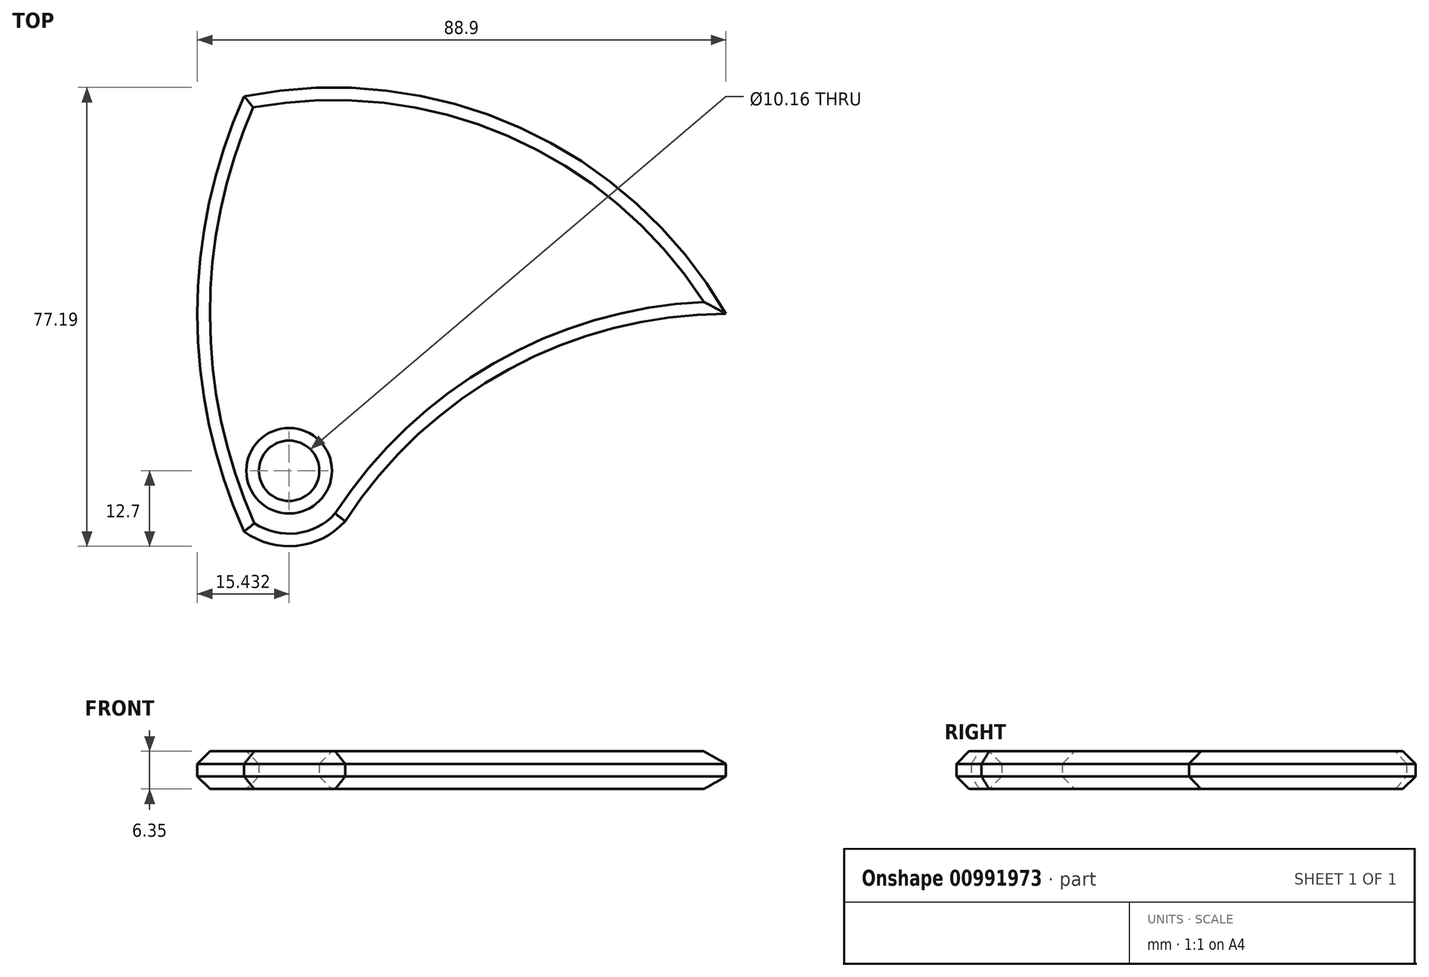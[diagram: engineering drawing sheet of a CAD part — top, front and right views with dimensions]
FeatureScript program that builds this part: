
annotation { "Feature Type Name" : "Feature", "Feature Type Description" : "" }
export const myFeature = defineFeature(function(context is Context, id is Id, definition is map)
    precondition{}
    {
        {
            var Q0;
            Q0=qCreatedBy(makeId("Top.planeOp"),FACE);
            var sketch = newSketch(context, id + "F0", { "sketchPlane" : qUnion([Q0])});
            skCircle(sketch, "E0", {"center": v(0, 0) * mm, "radius": 76.2 * mm});
            skArc(sketch, "E1", {"start": v(0, 0) * mm, "mid": v(10.2, 38.1) * mm, "end": v(0, 76.2) * mm});
            skLineSegment(sketch, "E2", {"start": v(0, 76.2) * mm, "end": v(0, 0) * mm, "construction": true});
            skLineSegment(sketch, "E3", {"start": v(0, 0) * mm, "end": v(66, 38.1) * mm, "construction": true});
            skLineSegment(sketch, "E4", {"start": v(0, 0) * mm, "end": v(66, -38.1) * mm, "construction": true});
            skLineSegment(sketch, "E5", {"start": v(0, 0) * mm, "end": v(0, -76.2) * mm, "construction": true});
            skLineSegment(sketch, "E6", {"start": v(0, 0) * mm, "end": v(-66, -38.1) * mm, "construction": true});
            skLineSegment(sketch, "E7", {"start": v(0, 0) * mm, "end": v(-66, 38.1) * mm, "construction": true});
            skArc(sketch, "E8", {"start": v(0, 0) * mm, "mid": v(38.1, 10.2) * mm, "end": v(66, 38.1) * mm});
            skArc(sketch, "E9", {"start": v(0, 0) * mm, "mid": v(27.9, -27.9) * mm, "end": v(66, -38.1) * mm});
            skArc(sketch, "E10", {"start": v(0, 0) * mm, "mid": v(-10.2, -38.1) * mm, "end": v(0, -76.2) * mm});
            skArc(sketch, "E11", {"start": v(0, 0) * mm, "mid": v(-38.1, -10.2) * mm, "end": v(-66, -38.1) * mm});
            skArc(sketch, "E12", {"start": v(0, 0) * mm, "mid": v(-27.9, 27.9) * mm, "end": v(-66, 38.1) * mm});
            skSolve(sketch);
        }
        {
            var Q0;
            Q0=qCreatedBy(makeId("Top.planeOp"),FACE);
            var sketch = newSketch(context, id + "F1", { "sketchPlane" : qUnion([Q0])});
            skCircle(sketch, "E13", {"center": v(0, 0) * mm, "radius": 76.2 * mm});
            skArc(sketch, "E14", {"start": v(-72.2, 51.86) * mm, "mid": v(-69.44, 44.82) * mm, "end": v(-66, 38.1) * mm, "construction": true});
            skArc(sketch, "E15", {"start": v(8.8, 88.46) * mm, "mid": v(4.1, 82.55) * mm, "end": v(0, 76.2) * mm, "construction": true});
            skArc(sketch, "E16", {"start": v(81.01, 36.6) * mm, "mid": v(73.54, 37.73) * mm, "end": v(66, 38.1) * mm, "construction": true});
            skArc(sketch, "E17", {"start": v(72.2, -51.86) * mm, "mid": v(69.44, -44.82) * mm, "end": v(66, -38.1) * mm, "construction": true});
            skArc(sketch, "E18", {"start": v(-8.8, -88.46) * mm, "mid": v(-4.1, -82.55) * mm, "end": v(0, -76.2) * mm, "construction": true});
            skArc(sketch, "E19", {"start": v(-81.01, -36.6) * mm, "mid": v(-73.54, -37.73) * mm, "end": v(-66, -38.1) * mm, "construction": true});
            skCircle(sketch, "E20", {"center": v(0, 0) * mm, "radius": 88.9 * mm, "construction": true});
            skArc(sketch, "E21.trimOffspring", {"start": v(0, 0) * mm, "mid": v(34.62, -31.34) * mm, "end": v(81.01, -36.6) * mm, "construction": true});
            skArc(sketch, "E22.trimOffspring", {"start": v(0, 0) * mm, "mid": v(-9.83, -45.65) * mm, "end": v(8.8, -88.46) * mm, "construction": true});
            skArc(sketch, "E23.trimOffspring", {"start": v(0, 0) * mm, "mid": v(-44.45, -14.3) * mm, "end": v(-72.2, -51.86) * mm, "construction": true});
            skArc(sketch, "E24.trimOffspring", {"start": v(0, 0) * mm, "mid": v(-34.62, 31.34) * mm, "end": v(-81.01, 36.6) * mm, "construction": true});
            skArc(sketch, "E25.trimOffspring", {"start": v(0, 0) * mm, "mid": v(9.83, 45.65) * mm, "end": v(-8.8, 88.46) * mm, "construction": true});
            skArc(sketch, "E26.trimOffspring", {"start": v(0, 0) * mm, "mid": v(44.45, 14.3) * mm, "end": v(72.2, 51.86) * mm, "construction": true});
            skLineSegment(sketch, "E27", {"start": v(0, 88.9) * mm, "end": v(0, 0) * mm, "construction": true});
            skLineSegment(sketch, "E28", {"start": v(-15.44, 87.55) * mm, "end": v(0, 0) * mm, "construction": true});
            skLineSegment(sketch, "E29", {"start": v(0, 0) * mm, "end": v(-83.54, 30.4) * mm, "construction": true});
            skLineSegment(sketch, "E30", {"start": v(0, 0) * mm, "end": v(-68.1, -57.14) * mm, "construction": true});
            skLineSegment(sketch, "E31", {"start": v(0, 0) * mm, "end": v(15.44, -87.55) * mm, "construction": true});
            skLineSegment(sketch, "E32", {"start": v(0, 0) * mm, "end": v(83.54, -30.4) * mm, "construction": true});
            skLineSegment(sketch, "E33", {"start": v(0, 0) * mm, "end": v(68.1, 57.14) * mm, "construction": true});
            skCircle(sketch, "E34", {"center": v(0, 0) * mm, "radius": 82.55 * mm, "construction": true});
            skArc(sketch, "E35", {"start": v(-60.5, -34.92) * mm, "mid": v(61.3, 33.48) * mm, "end": v(-62.08, -32.01) * mm, "construction": true});
            skLineSegment(sketch, "E36.0", {"start": v(0, 0) * mm, "end": v(-66, 38.1) * mm, "construction": true});
            skPoint(sketch, "E37.0", {"position": v(33, 19.05) * mm});
            skLineSegment(sketch, "E38.0", {"start": v(0, 0) * mm, "end": v(66, 38.1) * mm, "construction": true});
            skLineSegment(sketch, "E39.0", {"start": v(0, 0) * mm, "end": v(66, -38.1) * mm, "construction": true});
            skLineSegment(sketch, "E40.0", {"start": v(0, 0) * mm, "end": v(0, -76.2) * mm, "construction": true});
            skLineSegment(sketch, "E41.0", {"start": v(0, 0) * mm, "end": v(-66, -38.1) * mm, "construction": true});
            skLineSegment(sketch, "E42", {"start": v(-66, 38.1) * mm, "end": v(-76.99, 44.45) * mm, "construction": true});
            skArc(sketch, "E43", {"start": v(-72.2, 51.86) * mm, "mid": v(-68.78, 41.67) * mm, "end": v(-58.77, 37.76) * mm, "construction": true});
            skArc(sketch, "E44", {"start": v(8.8, 88.46) * mm, "mid": v(1.7, 80.4) * mm, "end": v(3.32, 69.77) * mm, "construction": true});
            skArc(sketch, "E45", {"start": v(81.01, 36.6) * mm, "mid": v(70.48, 38.73) * mm, "end": v(62.08, 32.01) * mm, "construction": true});
            skArc(sketch, "E46", {"start": v(72.2, -51.86) * mm, "mid": v(68.78, -41.67) * mm, "end": v(58.77, -37.76) * mm, "construction": true});
            skArc(sketch, "E47", {"start": v(-8.8, -88.46) * mm, "mid": v(-1.7, -80.4) * mm, "end": v(-3.32, -69.77) * mm, "construction": true});
            skArc(sketch, "E48", {"start": v(-81.01, -36.6) * mm, "mid": v(-70.48, -38.73) * mm, "end": v(-62.08, -32.01) * mm, "construction": true});
            skArc(sketch, "E49", {"start": v(0, 0) * mm, "mid": v(-44.45, -14.3) * mm, "end": v(-72.2, -51.86) * mm});
            skArc(sketch, "E50", {"start": v(-81.01, -36.6) * mm, "mid": v(-70.48, -38.73) * mm, "end": v(-62.08, -32.01) * mm});
            skArc(sketch, "E51", {"start": v(0, 0) * mm, "mid": v(-34.62, 31.34) * mm, "end": v(-81.01, 36.6) * mm});
            skArc(sketch, "E52", {"start": v(-81.01, 36.6) * mm, "mid": v(-88.46, -8.8) * mm, "end": v(-72.2, -51.86) * mm});
            skCircle(sketch, "E53", {"center": v(-73.47, -26.39) * mm, "radius": 5.08 * mm});
            skSolve(sketch);
        }
        {
            var Q0;
            {var subQ0=sQuery(id+"F1.wireOp",EDGE,"E51");var subQ1=sQuery(id+"F1.wireOp",EDGE,"E13");var subQ2=makeQuery(id+"F1.imprint","INTERSECT",VERTEX,{"derivedFrom":[subQ1,subQ0]});Q0=makeQuery(id+"F1.imprint","IMPRINT",FACE,{"disambiguationData":[TD([[makeQuery(id+"F1.imprint","IMPRINT",EDGE,{"disambiguationData":[TD([[subQ2,-1.0]])],"derivedFrom":subQ1}),-1.0]])]});}
            var Q1;
            {var subQ4=sQuery(id+"F1.wireOp",EDGE,"E13");var subQ6=sQuery(id+"F1.wireOp",EDGE,"E51");var subQ8=makeQuery(id+"F1.imprint","INTERSECT",VERTEX,{"derivedFrom":[subQ4,subQ6]});Q1=makeQuery(id+"F1.imprint","IMPRINT",FACE,{"disambiguationData":[TD([[makeQuery(id+"F1.imprint","IMPRINT",EDGE,{"disambiguationData":[TD([[subQ8,-1.0]])],"derivedFrom":subQ4}),1.0]])]});}
            extrude(context, id + "F2", {"entities" : qUnion([Q0, Q1]), "depth" : 6.35 * mm, "offsetDistance" : 25.4 * mm});
        }
        {
            var Q0;
            Q0=makeQuery(id+"F2.opExtrude","CAP_FACE",FACE,{"disambiguationData":[OSD([sQuery(id+"F1.wireOp",EDGE,"E49"),sQuery(id+"F1.wireOp",EDGE,"E50"),sQuery(id+"F1.wireOp",EDGE,"E51"),sQuery(id+"F1.wireOp",EDGE,"E52"),sQuery(id+"F1.wireOp",EDGE,"E53")])],"isStart":false});
            var Q1;
            Q1=makeQuery(id+"F2.opExtrude","CAP_FACE",FACE,{"disambiguationData":[OSD([sQuery(id+"F1.wireOp",EDGE,"E49"),sQuery(id+"F1.wireOp",EDGE,"E50"),sQuery(id+"F1.wireOp",EDGE,"E51"),sQuery(id+"F1.wireOp",EDGE,"E52"),sQuery(id+"F1.wireOp",EDGE,"E53")])],"isStart":true});
            chamfer(context, id + "F3", {"entities" : qUnion([Q0, Q1]), "width" : 2.12 * mm, "tangentPropagation" : true});
        }
    });
